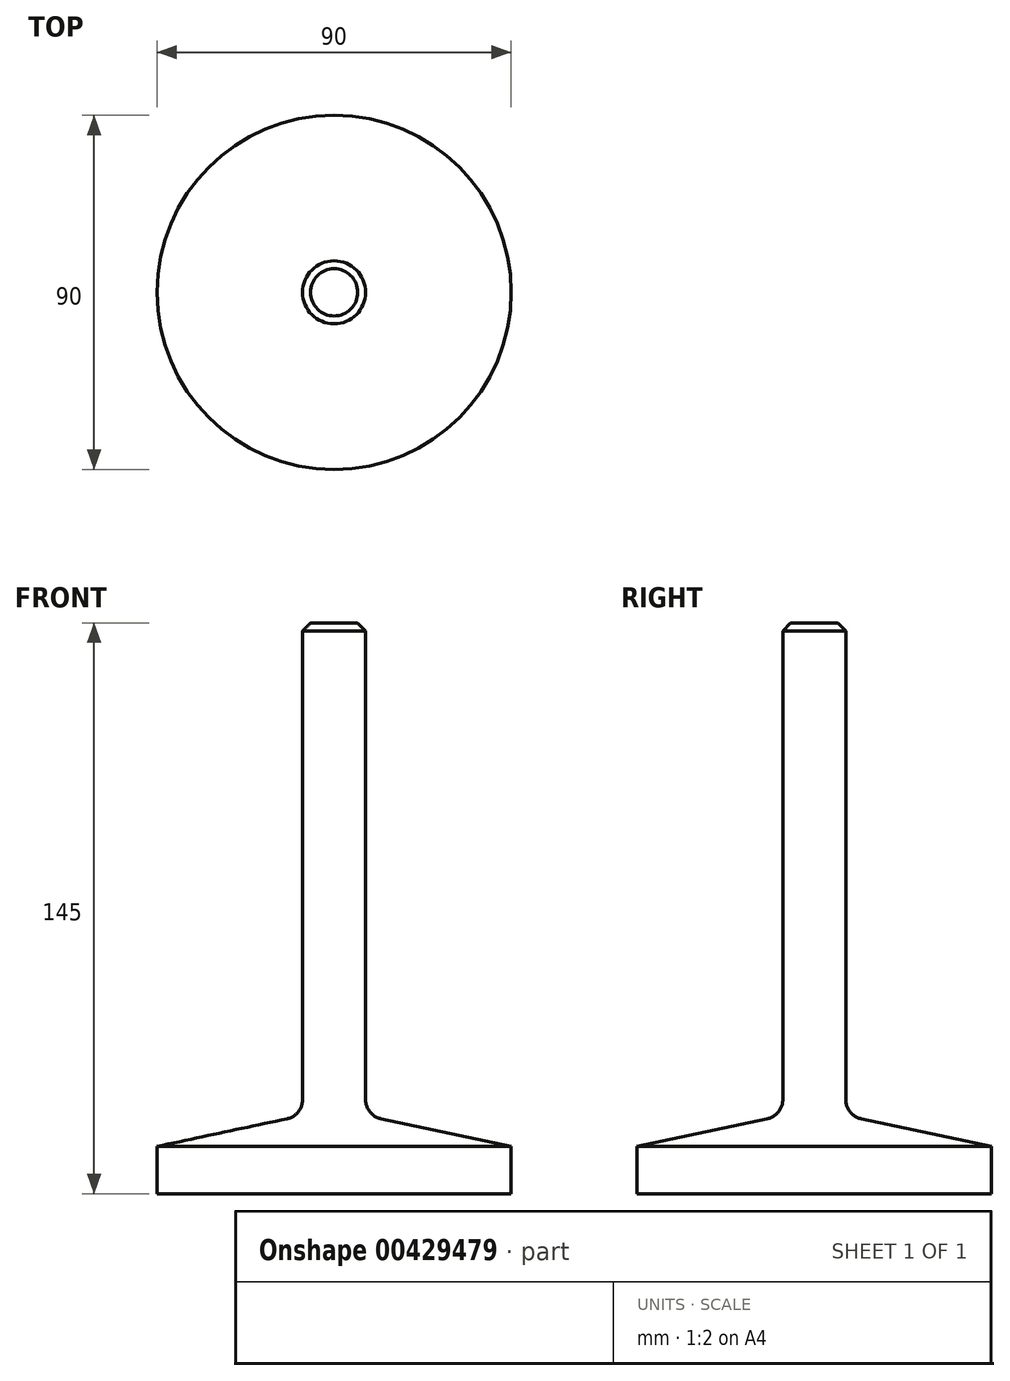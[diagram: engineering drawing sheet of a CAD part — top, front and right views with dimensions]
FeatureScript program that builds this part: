
annotation { "Feature Type Name" : "Feature", "Feature Type Description" : "" }
export const myFeature = defineFeature(function(context is Context, id is Id, definition is map)
    precondition{}
    {
        {
            var Q0;
            Q0=qCreatedBy(makeId("Front.planeOp"),FACE);
            var sketch = newSketch(context, id + "F0", { "sketchPlane" : qUnion([Q0])});
            skLineSegment(sketch, "E0", {"start": v(0, 0) * mm, "end": v(0, 88.35) * mm, "construction": true});
            skLineSegment(sketch, "E1", {"start": v(0, 145) * mm, "end": v(8, 145) * mm});
            skLineSegment(sketch, "E2", {"start": v(8, 145) * mm, "end": v(8, 19.86) * mm});
            skLineSegment(sketch, "E3", {"start": v(8, 19.86) * mm, "end": v(45, 12) * mm});
            skLineSegment(sketch, "E4", {"start": v(45, 12) * mm, "end": v(45, 0) * mm});
            skLineSegment(sketch, "E5", {"start": v(45, 0) * mm, "end": v(0, 0) * mm});
            skLineSegment(sketch, "E6", {"start": v(0, 0) * mm, "end": v(0, 145) * mm});
            skSolve(sketch);
        }
        {
            var Q0;
            Q0=makeQuery(id+"F0.imprint","IMPRINT",FACE,{"disambiguationData":[TD([[makeQuery(id+"F0.imprint","IMPRINT",EDGE,{"derivedFrom":sQuery(id+"F0.wireOp",EDGE,"E1")}),-1.0]])]});
            var Q1;
            Q1=sQuery(id+"F0.wireOp",EDGE,"E6");
            revolve(context, id + "F1", {"entities" : qUnion([Q0]), "axis" : qUnion([Q1]), "revolveType" : RevolveType.FULL});
        }
        {
            var Q0;
            Q0=makeQuery(id+"F1.opRevolve","SWEPT_EDGE",EDGE,{"disambiguationData":[OSD([sQuery(id+"F0.wireOp",EDGE,"E1"),sQuery(id+"F0.wireOp",EDGE,"E2")])]});
            chamfer(context, id + "F2", {"entities" : qUnion([Q0]), "width" : 2 * mm, "tangentPropagation" : true});
        }
        {
            var Q0;
            Q0=makeQuery(id+"F1.opRevolve","SWEPT_EDGE",EDGE,{"disambiguationData":[OSD([sQuery(id+"F0.wireOp",EDGE,"E2"),sQuery(id+"F0.wireOp",EDGE,"E3")])]});
            fillet(context, id + "F3", {"entities" : qUnion([Q0]), "radius" : 5 * mm, "tangentPropagation" : true, "allowEdgeOverflow" : false});
        }
    });
